# Revit family: Wall-Propeller-Fan_LJDB_A-B-Series_Carnes
name_source: partatom
category: Mechanical Equipment
revit_build: Autodesk Revit Architecture 2012 (Build: 20110916_2132(x64)
units: mm (PartAtom-declared; Revit-internal decimal feet)

## types (7) — shared parameters
04 CSI = 23 34 16
95 CSI = 15830
Assembly Code = D3040200
Catalog URL = http://www.carnes.com
Description = A & B Series Wall Propeller Fans
Housing = Aluminum-Carnes-Spun-Brushed
IOM Instructions URL = http://www.carnes.com
Manufacturer = Carnes Company
Manufacturer Fax = 608-845-6470
Product Page URL = http://www.carnes.com
Subcategory = Spun Aluminum Exhausters
URL = http://www.carnes.com
Warranty URL = http://www.carnes.com
ecoScorecard Product Page = http://ecoscorecard.com

## per-type parameters (varying)
| type | A | Blade Diameter | Blade Radius | C | F Diameter | F Radius | G | H | Support Width |
| LJDB 10 | 16" | 9 3/8" | 3 3/16" | 6" | 10 3/8" | 5 3/16" | 5" | 8" | 15 1/2" |
| LJDB 12 | 16" | 11 3/8" | 4 3/16" | 6" | 12 3/8" | 6 3/16" | 5" | 8" | 15 1/2" |
| LJDB 16 | 20" | 15 3/8" | 6 3/16" | 6" | 16 3/8" | 8 3/16" | 5" | 8" | 19 1/2" |
| LJDB 18 | 24" | 17 3/8" | 7 3/16" | 6" | 18 3/8" | 9 3/16" | 5" | 8" | 23 1/2" |
| LJDB 20 | 24" | 19 3/8" | 8 3/16" | 7" | 20 3/8" | 10 3/16" | 5" | 8" | 23 1/2" |
| LJDB 24 | 30" | 24" | 10 1/2" | 10" | 25" | 12 1/2" | 4" | 8 3/4" | 29 1/2" |
| LJDB 30 | 36" | 30" | 13 1/2" | 10" | 31" | 15 1/2" | 4" | 8 3/4" | 35 1/2" |

note: column(s) folded — value = type name in every type: Model

## geometry (parser evidence)
native form markers: Blend x6, Sweep x13
no freeform markers — native parametric forms only
